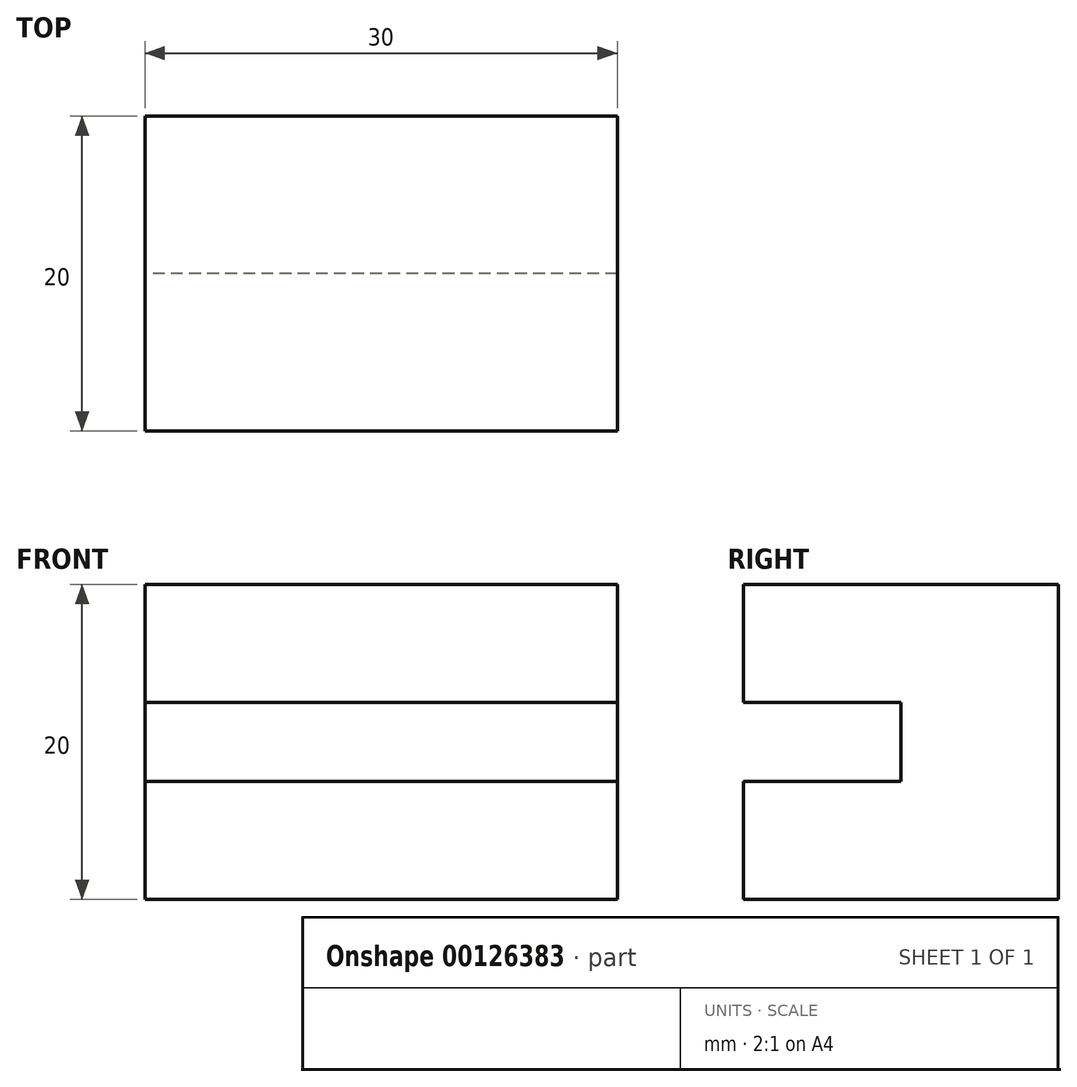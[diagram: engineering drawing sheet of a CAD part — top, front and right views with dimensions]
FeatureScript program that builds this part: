
annotation { "Feature Type Name" : "Feature", "Feature Type Description" : "" }
export const myFeature = defineFeature(function(context is Context, id is Id, definition is map)
    precondition{}
    {
        {
            var Q0;
            Q0=qCreatedBy(makeId("Right.planeOp"),FACE);
            var sketch = newSketch(context, id + "F0", { "sketchPlane" : qUnion([Q0])});
            skLineSegment(sketch, "E0", {"start": v(0, 0) * mm, "end": v(20, 0) * mm});
            skLineSegment(sketch, "E1", {"start": v(20, 0) * mm, "end": v(20, 20) * mm});
            skLineSegment(sketch, "E2", {"start": v(20, 20) * mm, "end": v(0, 20) * mm});
            skLineSegment(sketch, "E3", {"start": v(0, 20) * mm, "end": v(0, 12.5) * mm});
            skLineSegment(sketch, "E4", {"start": v(0, 12.5) * mm, "end": v(10, 12.5) * mm});
            skLineSegment(sketch, "E5", {"start": v(10, 12.5) * mm, "end": v(10, 7.5) * mm});
            skLineSegment(sketch, "E6", {"start": v(10, 7.5) * mm, "end": v(0, 7.5) * mm});
            skLineSegment(sketch, "E7", {"start": v(0, 7.5) * mm, "end": v(0, 0) * mm});
            skLineSegment(sketch, "E8", {"start": v(5, 20) * mm, "end": v(5, 12.5) * mm});
            skPoint(sketch, "E8.endSnap0", {"position": v(5, 12.5) * mm});
            skLineSegment(sketch, "E9", {"start": v(5, 15) * mm, "end": v(20, 15) * mm});
            skLineSegment(sketch, "E10", {"start": v(5, 7.5) * mm, "end": v(5, 0) * mm});
            skLineSegment(sketch, "E11", {"start": v(5, 5) * mm, "end": v(20, 5) * mm});
            skSolve(sketch);
        }
        {
            var Q0;
            Q0 = qSketchRegion(id + "F0", true);
            extrude(context, id + "F1", {"entities" : qUnion([Q0]), "depth" : 30 * mm});
        }
    });
